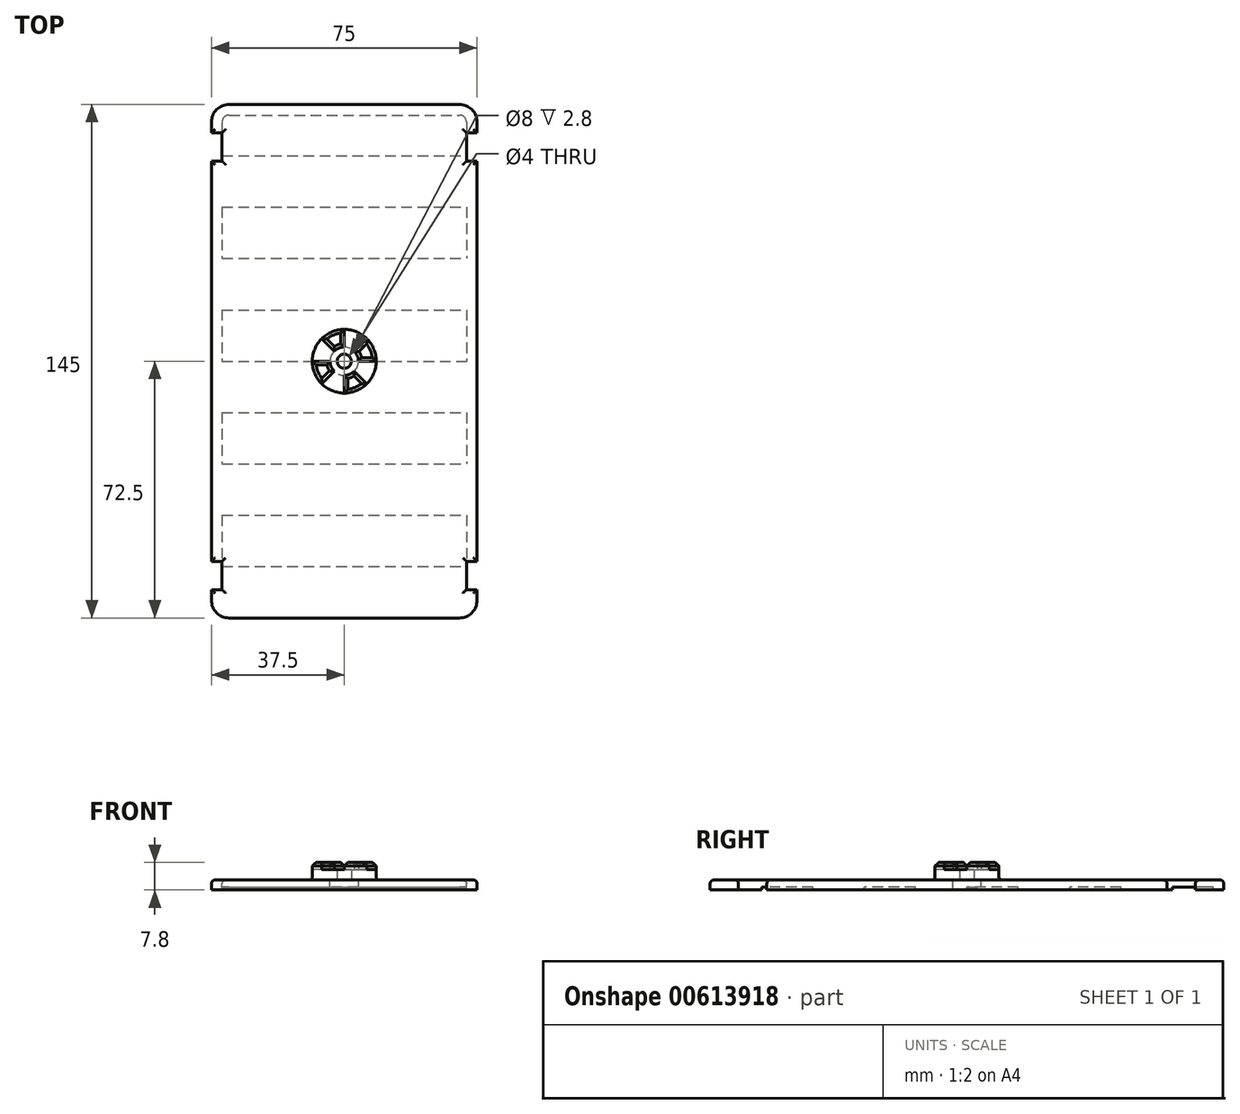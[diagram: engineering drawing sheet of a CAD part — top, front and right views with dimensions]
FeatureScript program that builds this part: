
annotation { "Feature Type Name" : "Feature", "Feature Type Description" : "" }
export const myFeature = defineFeature(function(context is Context, id is Id, definition is map)
    precondition{}
    {
        {
            var Q0;
            Q0=qCreatedBy(makeId("Top.planeOp"),FACE);
            var sketch = newSketch(context, id + "F0", { "sketchPlane" : qUnion([Q0])});
            skLineSegment(sketch, "E0.bottom", {"start": v(-32.5, 72.5) * mm, "end": v(32.5, 72.5) * mm});
            skLineSegment(sketch, "E0.top", {"start": v(-32.5, -72.5) * mm, "end": v(32.5, -72.5) * mm});
            skLineSegment(sketch, "E0.left", {"start": v(-37.5, 67.5) * mm, "end": v(-37.5, -67.5) * mm});
            skLineSegment(sketch, "E0.right", {"start": v(37.5, 67.5) * mm, "end": v(37.5, -67.5) * mm});
            skPoint(sketch, "E0.middle", {"position": v(0, 0) * mm});
            skLineSegment(sketch, "E1.0.1.0", {"start": v(-37.5, 58) * mm, "end": v(37.5, 58) * mm});
            skLineSegment(sketch, "E1.0.2.0", {"start": v(-37.5, 43.5) * mm, "end": v(37.5, 43.5) * mm});
            skLineSegment(sketch, "E1.0.3.0", {"start": v(-37.5, 29) * mm, "end": v(37.5, 29) * mm});
            skLineSegment(sketch, "E1.0.4.0", {"start": v(-37.5, 14.5) * mm, "end": v(37.5, 14.5) * mm});
            skLineSegment(sketch, "E1.0.5.0", {"start": v(-37.5, 0) * mm, "end": v(37.5, 0) * mm});
            skLineSegment(sketch, "E1.0.6.0", {"start": v(-37.5, -14.5) * mm, "end": v(37.5, -14.5) * mm});
            skLineSegment(sketch, "E1.0.7.0", {"start": v(-37.5, -29) * mm, "end": v(37.5, -29) * mm});
            skLineSegment(sketch, "E1.0.8.0", {"start": v(-37.5, -43.5) * mm, "end": v(37.5, -43.5) * mm});
            skLineSegment(sketch, "E1.0.9.0", {"start": v(-37.5, -58) * mm, "end": v(37.5, -58) * mm});
            skLineSegment(sketch, "E1.direction2", {"start": v(-37.5, 72.5) * mm, "end": v(-37.5, 58) * mm, "construction": true});
            skPoint(sketch, "E2.visualSharp", {"position": v(37.5, 72.5) * mm});
            skArc(sketch, "E2.filletArc", {"start": v(37.5, 67.5) * mm, "mid": v(36.04, 71.04) * mm, "end": v(32.5, 72.5) * mm});
            skPoint(sketch, "E3.visualSharp", {"position": v(-37.5, 72.5) * mm});
            skPoint(sketch, "E4.visualSharp", {"position": v(-37.5, -72.5) * mm});
            skArc(sketch, "E4.filletArc", {"start": v(-37.5, -67.5) * mm, "mid": v(-36.04, -71.04) * mm, "end": v(-32.5, -72.5) * mm});
            skPoint(sketch, "E5.visualSharp", {"position": v(37.5, -72.5) * mm});
            skArc(sketch, "E5.filletArc", {"start": v(32.5, -72.5) * mm, "mid": v(36.04, -71.04) * mm, "end": v(37.5, -67.5) * mm});
            skArc(sketch, "E6.filletArc", {"start": v(-32.5, 72.5) * mm, "mid": v(-36.04, 71.04) * mm, "end": v(-37.5, 67.5) * mm});
            skLineSegment(sketch, "E7.0", {"start": v(-34.5, 67.5) * mm, "end": v(-34.5, -67.5) * mm});
            skArc(sketch, "E7.1", {"start": v(-32.5, 69.5) * mm, "mid": v(-33.91, 68.91) * mm, "end": v(-34.5, 67.5) * mm});
            skArc(sketch, "E7.2", {"start": v(-34.5, -67.5) * mm, "mid": v(-33.91, -68.91) * mm, "end": v(-32.5, -69.5) * mm});
            skLineSegment(sketch, "E7.3", {"start": v(-32.5, 69.5) * mm, "end": v(32.5, 69.5) * mm});
            skLineSegment(sketch, "E7.4", {"start": v(-32.5, -69.5) * mm, "end": v(32.5, -69.5) * mm});
            skArc(sketch, "E7.5", {"start": v(32.5, -69.5) * mm, "mid": v(33.91, -68.91) * mm, "end": v(34.5, -67.5) * mm});
            skLineSegment(sketch, "E7.6", {"start": v(34.5, 67.5) * mm, "end": v(34.5, -67.5) * mm});
            skArc(sketch, "E7.7", {"start": v(34.5, 67.5) * mm, "mid": v(33.91, 68.91) * mm, "end": v(32.5, 69.5) * mm});
            skSolve(sketch);
        }
        {
            var Q0;
            {var subQ0=sQuery(id+"F0.wireOp",EDGE,"E1.0.3.0");Q0=makeQuery(id+"F0.imprint","IMPRINT",FACE,{"disambiguationData":[TD([[makeQuery(id+"F0.imprint","IMPRINT",EDGE,{"derivedFrom":subQ0}),-1.0]])]});}
            var Q1;
            {var subQ0=sQuery(id+"F0.wireOp",EDGE,"E1.0.5.0");Q1=makeQuery(id+"F0.imprint","IMPRINT",FACE,{"disambiguationData":[TD([[makeQuery(id+"F0.imprint","IMPRINT",EDGE,{"derivedFrom":subQ0}),-1.0]])]});}
            var Q2;
            {var subQ0=sQuery(id+"F0.wireOp",EDGE,"E1.0.7.0");Q2=makeQuery(id+"F0.imprint","IMPRINT",FACE,{"disambiguationData":[TD([[makeQuery(id+"F0.imprint","IMPRINT",EDGE,{"derivedFrom":subQ0}),-1.0]])]});}
            var Q3;
            {var subQ0=sQuery(id+"F0.wireOp",EDGE,"E0.top");Q3=makeQuery(id+"F0.imprint","IMPRINT",FACE,{"disambiguationData":[TD([[makeQuery(id+"F0.imprint","IMPRINT",EDGE,{"derivedFrom":subQ0}),1.0]])]});}
            var Q4;
            {var subQ0=sQuery(id+"F0.wireOp",EDGE,"E1.0.1.0");Q4=makeQuery(id+"F0.imprint","IMPRINT",FACE,{"disambiguationData":[TD([[makeQuery(id+"F0.imprint","IMPRINT",EDGE,{"derivedFrom":subQ0}),-1.0]])]});}
            var Q5;
            {var subQ0=sQuery(id+"F0.wireOp",EDGE,"E1.0.8.0");var subQ1=sQuery(id+"F0.wireOp",EDGE,"E0.left");var subQ2=makeQuery(id+"F0.imprint","INTERSECT",VERTEX,{"derivedFrom":[subQ1,subQ0]});Q5=makeQuery(id+"F0.imprint","IMPRINT",FACE,{"disambiguationData":[TD([[makeQuery(id+"F0.imprint","IMPRINT",EDGE,{"disambiguationData":[TD([[subQ2,-1.0]])],"derivedFrom":subQ1}),1.0]])]});}
            var Q6;
            {var subQ0=sQuery(id+"F0.wireOp",EDGE,"E1.0.8.0");var subQ1=sQuery(id+"F0.wireOp",EDGE,"E0.right");var subQ2=makeQuery(id+"F0.imprint","INTERSECT",VERTEX,{"derivedFrom":[subQ1,subQ0]});Q6=makeQuery(id+"F0.imprint","IMPRINT",FACE,{"disambiguationData":[TD([[makeQuery(id+"F0.imprint","IMPRINT",EDGE,{"disambiguationData":[TD([[subQ2,-1.0]])],"derivedFrom":subQ1}),-1.0]])]});}
            var Q7;
            {var subQ4=sQuery(id+"F0.wireOp",EDGE,"E7.2");Q7=makeQuery(id+"F0.imprint","IMPRINT",FACE,{"disambiguationData":[TD([[makeQuery(id+"F0.imprint","IMPRINT",EDGE,{"derivedFrom":subQ4}),1.0]])]});}
            var Q8;
            {var subQ0=sQuery(id+"F0.wireOp",EDGE,"E1.0.6.0");var subQ1=sQuery(id+"F0.wireOp",EDGE,"E0.right");var subQ2=makeQuery(id+"F0.imprint","INTERSECT",VERTEX,{"derivedFrom":[subQ1,subQ0]});Q8=makeQuery(id+"F0.imprint","IMPRINT",FACE,{"disambiguationData":[TD([[makeQuery(id+"F0.imprint","IMPRINT",EDGE,{"disambiguationData":[TD([[subQ2,-1.0]])],"derivedFrom":subQ1}),-1.0]])]});}
            var Q9;
            {var subQ0=sQuery(id+"F0.wireOp",EDGE,"E1.0.6.0");var subQ1=sQuery(id+"F0.wireOp",EDGE,"E0.left");var subQ2=makeQuery(id+"F0.imprint","INTERSECT",VERTEX,{"derivedFrom":[subQ1,subQ0]});Q9=makeQuery(id+"F0.imprint","IMPRINT",FACE,{"disambiguationData":[TD([[makeQuery(id+"F0.imprint","IMPRINT",EDGE,{"disambiguationData":[TD([[subQ2,-1.0]])],"derivedFrom":subQ1}),1.0]])]});}
            var Q10;
            {var subQ0=sQuery(id+"F0.wireOp",EDGE,"E1.0.4.0");var subQ1=sQuery(id+"F0.wireOp",EDGE,"E0.left");var subQ2=makeQuery(id+"F0.imprint","INTERSECT",VERTEX,{"derivedFrom":[subQ1,subQ0]});Q10=makeQuery(id+"F0.imprint","IMPRINT",FACE,{"disambiguationData":[TD([[makeQuery(id+"F0.imprint","IMPRINT",EDGE,{"disambiguationData":[TD([[subQ2,-1.0]])],"derivedFrom":subQ1}),1.0]])]});}
            var Q11;
            {var subQ0=sQuery(id+"F0.wireOp",EDGE,"E1.0.2.0");var subQ1=sQuery(id+"F0.wireOp",EDGE,"E0.left");var subQ2=makeQuery(id+"F0.imprint","INTERSECT",VERTEX,{"derivedFrom":[subQ1,subQ0]});Q11=makeQuery(id+"F0.imprint","IMPRINT",FACE,{"disambiguationData":[TD([[makeQuery(id+"F0.imprint","IMPRINT",EDGE,{"disambiguationData":[TD([[subQ2,-1.0]])],"derivedFrom":subQ1}),1.0]])]});}
            var Q12;
            Q12=makeQuery(id+"F0.imprint","IMPRINT",FACE,{"disambiguationData":[TD([[makeQuery(id+"F0.imprint","IMPRINT",EDGE,{"derivedFrom":sQuery(id+"F0.wireOp",EDGE,"E0.bottom")}),-1.0]])]});
            var Q13;
            {var subQ0=sQuery(id+"F0.wireOp",EDGE,"E1.0.4.0");var subQ1=sQuery(id+"F0.wireOp",EDGE,"E0.right");var subQ2=makeQuery(id+"F0.imprint","INTERSECT",VERTEX,{"derivedFrom":[subQ1,subQ0]});Q13=makeQuery(id+"F0.imprint","IMPRINT",FACE,{"disambiguationData":[TD([[makeQuery(id+"F0.imprint","IMPRINT",EDGE,{"disambiguationData":[TD([[subQ2,-1.0]])],"derivedFrom":subQ1}),-1.0]])]});}
            var Q14;
            {var subQ0=sQuery(id+"F0.wireOp",EDGE,"E1.0.2.0");var subQ1=sQuery(id+"F0.wireOp",EDGE,"E0.right");var subQ2=makeQuery(id+"F0.imprint","INTERSECT",VERTEX,{"derivedFrom":[subQ1,subQ0]});Q14=makeQuery(id+"F0.imprint","IMPRINT",FACE,{"disambiguationData":[TD([[makeQuery(id+"F0.imprint","IMPRINT",EDGE,{"disambiguationData":[TD([[subQ2,-1.0]])],"derivedFrom":subQ1}),-1.0]])]});}
            extrude(context, id + "F1", {"entities" : qUnion([Q0, Q1, Q2, Q3, Q4, Q5, Q6, Q7, Q8, Q9, Q10, Q11, Q12, Q13, Q14]), "depth" : -0.8 * mm, "offsetDistance" : 25 * mm});
        }
        {
            var Q0;
            Q0 = qSketchRegion(id + "F0", true);
            var Q1;
            {var subQ0=sQuery(id+"F0.wireOp",EDGE,"E7.1");Q1=makeQuery(id+"F0.imprint","IMPRINT",FACE,{"disambiguationData":[TD([[makeQuery(id+"F0.imprint","IMPRINT",EDGE,{"derivedFrom":subQ0}),1.0]])]});}
            var Q2;
            {var subQ0=sQuery(id+"F0.wireOp",EDGE,"E7.0");var subQ1=sQuery(id+"F0.wireOp",EDGE,"E1.0.2.0");var subQ2=makeQuery(id+"F0.imprint","INTERSECT",VERTEX,{"derivedFrom":[subQ1,subQ0]});Q2=makeQuery(id+"F0.imprint","IMPRINT",FACE,{"disambiguationData":[TD([[makeQuery(id+"F0.imprint","IMPRINT",EDGE,{"disambiguationData":[TD([[subQ2,-1.0]])],"derivedFrom":subQ1}),-1.0]])]});}
            var Q3;
            {var subQ0=sQuery(id+"F0.wireOp",EDGE,"E7.0");var subQ1=sQuery(id+"F0.wireOp",EDGE,"E1.0.1.0");var subQ2=makeQuery(id+"F0.imprint","INTERSECT",VERTEX,{"derivedFrom":[subQ1,subQ0]});Q3=makeQuery(id+"F0.imprint","IMPRINT",FACE,{"disambiguationData":[TD([[makeQuery(id+"F0.imprint","IMPRINT",EDGE,{"disambiguationData":[TD([[subQ2,-1.0]])],"derivedFrom":subQ1}),-1.0]])]});}
            var Q4;
            {var subQ0=sQuery(id+"F0.wireOp",EDGE,"E7.0");var subQ1=sQuery(id+"F0.wireOp",EDGE,"E1.0.3.0");var subQ2=makeQuery(id+"F0.imprint","INTERSECT",VERTEX,{"derivedFrom":[subQ1,subQ0]});Q4=makeQuery(id+"F0.imprint","IMPRINT",FACE,{"disambiguationData":[TD([[makeQuery(id+"F0.imprint","IMPRINT",EDGE,{"disambiguationData":[TD([[subQ2,-1.0]])],"derivedFrom":subQ1}),-1.0]])]});}
            var Q5;
            {var subQ0=sQuery(id+"F0.wireOp",EDGE,"E7.0");var subQ1=sQuery(id+"F0.wireOp",EDGE,"E1.0.4.0");var subQ2=makeQuery(id+"F0.imprint","INTERSECT",VERTEX,{"derivedFrom":[subQ1,subQ0]});Q5=makeQuery(id+"F0.imprint","IMPRINT",FACE,{"disambiguationData":[TD([[makeQuery(id+"F0.imprint","IMPRINT",EDGE,{"disambiguationData":[TD([[subQ2,-1.0]])],"derivedFrom":subQ1}),-1.0]])]});}
            var Q6;
            {var subQ0=sQuery(id+"F0.wireOp",EDGE,"E7.0");var subQ1=sQuery(id+"F0.wireOp",EDGE,"E1.0.5.0");var subQ2=makeQuery(id+"F0.imprint","INTERSECT",VERTEX,{"derivedFrom":[subQ1,subQ0]});Q6=makeQuery(id+"F0.imprint","IMPRINT",FACE,{"disambiguationData":[TD([[makeQuery(id+"F0.imprint","IMPRINT",EDGE,{"disambiguationData":[TD([[subQ2,-1.0]])],"derivedFrom":subQ1}),-1.0]])]});}
            var Q7;
            {var subQ4=sQuery(id+"F0.wireOp",EDGE,"E7.2");Q7=makeQuery(id+"F0.imprint","IMPRINT",FACE,{"disambiguationData":[TD([[makeQuery(id+"F0.imprint","IMPRINT",EDGE,{"derivedFrom":subQ4}),1.0]])]});}
            var Q8;
            {var subQ0=sQuery(id+"F0.wireOp",EDGE,"E7.0");var subQ1=sQuery(id+"F0.wireOp",EDGE,"E1.0.8.0");var subQ2=makeQuery(id+"F0.imprint","INTERSECT",VERTEX,{"derivedFrom":[subQ1,subQ0]});Q8=makeQuery(id+"F0.imprint","IMPRINT",FACE,{"disambiguationData":[TD([[makeQuery(id+"F0.imprint","IMPRINT",EDGE,{"disambiguationData":[TD([[subQ2,-1.0]])],"derivedFrom":subQ1}),-1.0]])]});}
            var Q9;
            {var subQ0=sQuery(id+"F0.wireOp",EDGE,"E7.0");var subQ1=sQuery(id+"F0.wireOp",EDGE,"E1.0.7.0");var subQ2=makeQuery(id+"F0.imprint","INTERSECT",VERTEX,{"derivedFrom":[subQ1,subQ0]});Q9=makeQuery(id+"F0.imprint","IMPRINT",FACE,{"disambiguationData":[TD([[makeQuery(id+"F0.imprint","IMPRINT",EDGE,{"disambiguationData":[TD([[subQ2,-1.0]])],"derivedFrom":subQ1}),-1.0]])]});}
            var Q10;
            {var subQ0=sQuery(id+"F0.wireOp",EDGE,"E7.0");var subQ1=sQuery(id+"F0.wireOp",EDGE,"E1.0.6.0");var subQ2=makeQuery(id+"F0.imprint","INTERSECT",VERTEX,{"derivedFrom":[subQ1,subQ0]});Q10=makeQuery(id+"F0.imprint","IMPRINT",FACE,{"disambiguationData":[TD([[makeQuery(id+"F0.imprint","IMPRINT",EDGE,{"disambiguationData":[TD([[subQ2,-1.0]])],"derivedFrom":subQ1}),-1.0]])]});}
            extrude(context, id + "F2", {"entities" : qUnion([Q0, Q1, Q2, Q3, Q4, Q5, Q6, Q7, Q8, Q9, Q10]), "operationType" : NewBodyOperationType.ADD, "depth" : 2 * mm, "offsetDistance" : 25 * mm});
        }
        {
            var Q0;
            Q0=makeQuery(id+"F2.opExtrude","CAP_FACE",FACE,{"disambiguationData":[OSD([sQuery(id+"F0.wireOp",EDGE,"E0.bottom"),sQuery(id+"F0.wireOp",EDGE,"E0.top"),sQuery(id+"F0.wireOp",EDGE,"E0.left"),sQuery(id+"F0.wireOp",EDGE,"E0.right")])],"isStart":false});
            var sketch = newSketch(context, id + "F3", { "sketchPlane" : qUnion([Q0])});
            skLineSegment(sketch, "E8.0", {"start": v(-37.5, 67.5) * mm, "end": v(-37.5, -67.5) * mm});
            skLineSegment(sketch, "E9.0", {"start": v(-32.5, 72.5) * mm, "end": v(32.5, 72.5) * mm});
            skLineSegment(sketch, "E10.0", {"start": v(37.5, 67.5) * mm, "end": v(37.5, -67.5) * mm});
            skLineSegment(sketch, "E11.0", {"start": v(-32.5, -72.5) * mm, "end": v(32.5, -72.5) * mm});
            skLineSegment(sketch, "E12.bottom", {"start": v(-29.5, -72.5) * mm, "end": v(-21.5, -72.5) * mm});
            skLineSegment(sketch, "E12.top", {"start": v(-29.5, -69.5) * mm, "end": v(-21.5, -69.5) * mm});
            skLineSegment(sketch, "E12.left", {"start": v(-29.5, -72.5) * mm, "end": v(-29.5, -69.5) * mm});
            skLineSegment(sketch, "E12.right", {"start": v(-21.5, -72.5) * mm, "end": v(-21.5, -69.5) * mm});
            skLineSegment(sketch, "E13.bottom", {"start": v(21.5, -72.5) * mm, "end": v(29.5, -72.5) * mm});
            skLineSegment(sketch, "E13.top", {"start": v(21.5, -69.5) * mm, "end": v(29.5, -69.5) * mm});
            skLineSegment(sketch, "E13.left", {"start": v(21.5, -72.5) * mm, "end": v(21.5, -69.5) * mm});
            skLineSegment(sketch, "E13.right", {"start": v(29.5, -72.5) * mm, "end": v(29.5, -69.5) * mm});
            skLineSegment(sketch, "E14.bottom", {"start": v(37.5, -64.5) * mm, "end": v(34.5, -64.5) * mm});
            skLineSegment(sketch, "E14.top", {"start": v(37.5, -56.5) * mm, "end": v(34.5, -56.5) * mm});
            skLineSegment(sketch, "E14.left", {"start": v(37.5, -64.5) * mm, "end": v(37.5, -56.5) * mm});
            skLineSegment(sketch, "E14.right", {"start": v(34.5, -64.5) * mm, "end": v(34.5, -56.5) * mm});
            skLineSegment(sketch, "E15.bottom", {"start": v(-37.5, -64.5) * mm, "end": v(-34.5, -64.5) * mm});
            skLineSegment(sketch, "E15.top", {"start": v(-37.5, -56.5) * mm, "end": v(-34.5, -56.5) * mm});
            skLineSegment(sketch, "E15.left", {"start": v(-37.5, -64.5) * mm, "end": v(-37.5, -56.5) * mm});
            skLineSegment(sketch, "E15.right", {"start": v(-34.5, -64.5) * mm, "end": v(-34.5, -56.5) * mm});
            skLineSegment(sketch, "E16.bottom", {"start": v(-37.5, 56.5) * mm, "end": v(-34.5, 56.5) * mm});
            skLineSegment(sketch, "E16.top", {"start": v(-37.5, 64.5) * mm, "end": v(-34.5, 64.5) * mm});
            skLineSegment(sketch, "E16.left", {"start": v(-37.5, 56.5) * mm, "end": v(-37.5, 64.5) * mm});
            skLineSegment(sketch, "E16.right", {"start": v(-34.5, 56.5) * mm, "end": v(-34.5, 64.5) * mm});
            skLineSegment(sketch, "E17.bottom", {"start": v(-29.5, 72.5) * mm, "end": v(-21.5, 72.5) * mm});
            skLineSegment(sketch, "E17.top", {"start": v(-29.5, 69.5) * mm, "end": v(-21.5, 69.5) * mm});
            skLineSegment(sketch, "E17.left", {"start": v(-29.5, 72.5) * mm, "end": v(-29.5, 69.5) * mm});
            skLineSegment(sketch, "E17.right", {"start": v(-21.5, 72.5) * mm, "end": v(-21.5, 69.5) * mm});
            skLineSegment(sketch, "E18.bottom", {"start": v(21.5, 72.5) * mm, "end": v(29.5, 72.5) * mm});
            skLineSegment(sketch, "E18.top", {"start": v(21.5, 69.5) * mm, "end": v(29.5, 69.5) * mm});
            skLineSegment(sketch, "E18.left", {"start": v(21.5, 72.5) * mm, "end": v(21.5, 69.5) * mm});
            skLineSegment(sketch, "E18.right", {"start": v(29.5, 72.5) * mm, "end": v(29.5, 69.5) * mm});
            skCircle(sketch, "E19", {"center": v(0, 0) * mm, "radius": 2 * mm});
            skCircle(sketch, "E20", {"center": v(0, 0) * mm, "radius": 4 * mm});
            skCircle(sketch, "E21", {"center": v(0, 0) * mm, "radius": 9 * mm});
            skLineSegment(sketch, "E22.bottom", {"start": v(37.5, 64.5) * mm, "end": v(34.5, 64.5) * mm});
            skLineSegment(sketch, "E22.top", {"start": v(37.5, 56.5) * mm, "end": v(34.5, 56.5) * mm});
            skLineSegment(sketch, "E22.left", {"start": v(37.5, 64.5) * mm, "end": v(37.5, 56.5) * mm});
            skLineSegment(sketch, "E22.right", {"start": v(34.5, 64.5) * mm, "end": v(34.5, 56.5) * mm});
            skSolve(sketch);
        }
        {
            var Q0;
            Q0=makeQuery(id+"F3.imprint","IMPRINT",FACE,{"disambiguationData":[TD([[makeQuery(id+"F3.imprint","IMPRINT",EDGE,{"derivedFrom":sQuery(id+"F3.wireOp",EDGE,"E13.bottom")}),1.0]])]});
            var Q1;
            Q1=makeQuery(id+"F3.imprint","IMPRINT",FACE,{"disambiguationData":[TD([[makeQuery(id+"F3.imprint","IMPRINT",EDGE,{"derivedFrom":sQuery(id+"F3.wireOp",EDGE,"E14.bottom")}),-1.0]])]});
            var Q2;
            Q2=makeQuery(id+"F3.imprint","IMPRINT",FACE,{"disambiguationData":[TD([[makeQuery(id+"F3.imprint","IMPRINT",EDGE,{"derivedFrom":sQuery(id+"F3.wireOp",EDGE,"E15.bottom")}),1.0]])]});
            var Q3;
            Q3=makeQuery(id+"F3.imprint","IMPRINT",FACE,{"disambiguationData":[TD([[makeQuery(id+"F3.imprint","IMPRINT",EDGE,{"derivedFrom":sQuery(id+"F3.wireOp",EDGE,"E12.bottom")}),1.0]])]});
            var Q4;
            Q4=makeQuery(id+"F3.imprint","IMPRINT",FACE,{"disambiguationData":[TD([[makeQuery(id+"F3.imprint","IMPRINT",EDGE,{"derivedFrom":sQuery(id+"F3.wireOp",EDGE,"E18.bottom")}),-1.0]])]});
            var Q5;
            Q5=makeQuery(id+"F3.imprint","IMPRINT",FACE,{"disambiguationData":[TD([[makeQuery(id+"F3.imprint","IMPRINT",EDGE,{"derivedFrom":sQuery(id+"F3.wireOp",EDGE,"B49sznqi-fGRp-VqjG-tYYg-6xHxRTEvqkHY.bottom")}),1.0]])]});
            var Q6;
            Q6=makeQuery(id+"F3.imprint","IMPRINT",FACE,{"disambiguationData":[TD([[makeQuery(id+"F3.imprint","IMPRINT",EDGE,{"derivedFrom":sQuery(id+"F3.wireOp",EDGE,"E17.bottom")}),-1.0]])]});
            var Q7;
            Q7=makeQuery(id+"F3.imprint","IMPRINT",FACE,{"disambiguationData":[TD([[makeQuery(id+"F3.imprint","IMPRINT",EDGE,{"derivedFrom":sQuery(id+"F3.wireOp",EDGE,"E16.bottom")}),1.0]])]});
            var Q8;
            Q8=makeQuery(id+"F3.imprint","IMPRINT",FACE,{"disambiguationData":[TD([[makeQuery(id+"F3.imprint","IMPRINT",EDGE,{"derivedFrom":sQuery(id+"F3.wireOp",EDGE,"E19")}),-1.0]])]});
            var Q9;
            Q9=makeQuery(id+"F3.imprint","IMPRINT",FACE,{"disambiguationData":[TD([[makeQuery(id+"F3.imprint","IMPRINT",EDGE,{"derivedFrom":sQuery(id+"F3.wireOp",EDGE,"E19")}),1.0]])]});
            var Q10;
            Q10=makeQuery(id+"F3.imprint","IMPRINT",FACE,{"disambiguationData":[TD([[makeQuery(id+"F3.imprint","IMPRINT",EDGE,{"derivedFrom":sQuery(id+"F3.wireOp",EDGE,"E22.bottom")}),1.0]])]});
            extrude(context, id + "F4", {"entities" : qUnion([Q0, Q1, Q2, Q3, Q4, Q5, Q6, Q7, Q8, Q9, Q10]), "operationType" : NewBodyOperationType.REMOVE, "oppositeDirection" : true, "depth" : 5 * mm, "offsetDistance" : 25 * mm});
        }
        {
            var Q0;
            Q0=makeQuery(id+"F3.imprint","IMPRINT",FACE,{"disambiguationData":[TD([[makeQuery(id+"F3.imprint","IMPRINT",EDGE,{"derivedFrom":sQuery(id+"F3.wireOp",EDGE,"E20")}),-1.0]])]});
            var Q1;
            Q1=makeQuery(id+"F3.imprint","IMPRINT",FACE,{"disambiguationData":[TD([[makeQuery(id+"F3.imprint","IMPRINT",EDGE,{"derivedFrom":sQuery(id+"F3.wireOp",EDGE,"E19")}),-1.0]])]});
            extrude(context, id + "F5", {"entities" : qUnion([Q0, Q1]), "operationType" : NewBodyOperationType.ADD, "depth" : 3 * mm, "offsetDistance" : 25 * mm});
        }
        {
            var Q0;
            Q0=makeQuery(id+"F5.opExtrude","CAP_FACE",FACE,{"disambiguationData":[OSD([sQuery(id+"F3.wireOp",EDGE,"E20"),sQuery(id+"F3.wireOp",EDGE,"E21")])],"isStart":false});
            var sketch = newSketch(context, id + "F6", { "sketchPlane" : qUnion([Q0])});
            skCircle(sketch, "E23.0", {"center": v(0, 0) * mm, "radius": 9 * mm});
            skCircle(sketch, "E24.0", {"center": v(0, 0) * mm, "radius": 4 * mm});
            skLineSegment(sketch, "E25", {"start": v(0, 4) * mm, "end": v(0, 9) * mm});
            skLineSegment(sketch, "E26.1.0", {"start": v(-2.83, 2.83) * mm, "end": v(-6.36, 6.36) * mm});
            skLineSegment(sketch, "E26.2.0", {"start": v(-4, 0) * mm, "end": v(-9, 0) * mm});
            skLineSegment(sketch, "E26.3.0", {"start": v(-2.83, -2.83) * mm, "end": v(-6.36, -6.36) * mm});
            skLineSegment(sketch, "E26.4.0", {"start": v(0, -4) * mm, "end": v(0, -9) * mm});
            skLineSegment(sketch, "E26.5.0", {"start": v(2.83, -2.83) * mm, "end": v(6.36, -6.36) * mm});
            skLineSegment(sketch, "E26.6.0", {"start": v(4, 0) * mm, "end": v(9, 0) * mm});
            skLineSegment(sketch, "E26.7.0", {"start": v(2.83, 2.83) * mm, "end": v(6.36, 6.36) * mm});
            skSolve(sketch);
        }
        {
            var Q0;
            {var subQ0=sQuery(id+"F6.wireOp",EDGE,"E26.6.0");Q0=makeQuery(id+"F6.imprint","IMPRINT",FACE,{"disambiguationData":[TD([[makeQuery(id+"F6.imprint","IMPRINT",EDGE,{"derivedFrom":subQ0}),1.0]])]});}
            var Q1;
            {var subQ0=sQuery(id+"F6.wireOp",EDGE,"E26.4.0");Q1=makeQuery(id+"F6.imprint","IMPRINT",FACE,{"disambiguationData":[TD([[makeQuery(id+"F6.imprint","IMPRINT",EDGE,{"derivedFrom":subQ0}),1.0]])]});}
            var Q2;
            {var subQ0=sQuery(id+"F6.wireOp",EDGE,"E25");Q2=makeQuery(id+"F6.imprint","IMPRINT",FACE,{"disambiguationData":[TD([[makeQuery(id+"F6.imprint","IMPRINT",EDGE,{"derivedFrom":subQ0}),1.0]])]});}
            var Q3;
            {var subQ0=sQuery(id+"F6.wireOp",EDGE,"E26.2.0");Q3=makeQuery(id+"F6.imprint","IMPRINT",FACE,{"disambiguationData":[TD([[makeQuery(id+"F6.imprint","IMPRINT",EDGE,{"derivedFrom":subQ0}),1.0]])]});}
            extrude(context, id + "F7", {"entities" : qUnion([Q0, Q1, Q2, Q3]), "operationType" : NewBodyOperationType.ADD, "depth" : 2 * mm, "offsetDistance" : 25 * mm});
        }
        {
            var Q0;
            Q0=makeQuery(id+"F7.opExtrude","CAP_EDGE",EDGE,{"disambiguationData":[OSD([sQuery(id+"F6.wireOp",EDGE,"E26.1.0")])],"isStart":false});
            var Q1;
            Q1=makeQuery(id+"F7.opExtrude","CAP_EDGE",EDGE,{"disambiguationData":[OSD([sQuery(id+"F6.wireOp",EDGE,"E25")])],"isStart":false});
            var Q2;
            Q2=makeQuery(id+"F7.opExtrude","CAP_EDGE",EDGE,{"disambiguationData":[OSD([sQuery(id+"F6.wireOp",EDGE,"E26.7.0")])],"isStart":false});
            var Q3;
            Q3=makeQuery(id+"F7.opExtrude","CAP_EDGE",EDGE,{"disambiguationData":[OSD([sQuery(id+"F6.wireOp",EDGE,"E26.6.0")])],"isStart":false});
            var Q4;
            Q4=makeQuery(id+"F7.opExtrude","CAP_EDGE",EDGE,{"disambiguationData":[OSD([sQuery(id+"F6.wireOp",EDGE,"E26.5.0")])],"isStart":false});
            var Q5;
            Q5=makeQuery(id+"F7.opExtrude","CAP_EDGE",EDGE,{"disambiguationData":[OSD([sQuery(id+"F6.wireOp",EDGE,"E26.4.0")])],"isStart":false});
            var Q6;
            Q6=makeQuery(id+"F7.opExtrude","CAP_EDGE",EDGE,{"disambiguationData":[OSD([sQuery(id+"F6.wireOp",EDGE,"E26.3.0")])],"isStart":false});
            var Q7;
            Q7=makeQuery(id+"F7.opExtrude","CAP_EDGE",EDGE,{"disambiguationData":[OSD([sQuery(id+"F6.wireOp",EDGE,"E26.2.0")])],"isStart":false});
            var Q8;
            {var subQ0=sQuery(id+"F6.wireOp",EDGE,"E23.0");Q8=makeQuery(id+"F7.opExtrude","CAP_EDGE",EDGE,{"disambiguationData":[OSD([subQ0]),TDD([makeQuery(id+"F6.imprint","IMPRINT",EDGE,{"disambiguationData":[TD([[makeQuery(id+"F6.imprint","INTERSECT",VERTEX,{"derivedFrom":[subQ0,sQuery(id+"F6.wireOp",EDGE,"E26.6.0")]}),-1.0]])],"derivedFrom":subQ0})])],"isStart":false});}
            var Q9;
            {var subQ0=sQuery(id+"F6.wireOp",EDGE,"E24.0");Q9=makeQuery(id+"F7.opExtrude","CAP_EDGE",EDGE,{"disambiguationData":[OSD([subQ0]),TDD([makeQuery(id+"F6.imprint","IMPRINT",EDGE,{"disambiguationData":[TD([[makeQuery(id+"F6.imprint","INTERSECT",VERTEX,{"derivedFrom":[subQ0,sQuery(id+"F6.wireOp",EDGE,"E26.6.0")]}),-1.0]])],"derivedFrom":subQ0})])],"isStart":false});}
            var Q10;
            {var subQ0=sQuery(id+"F6.wireOp",EDGE,"E24.0");Q10=makeQuery(id+"F7.opExtrude","CAP_EDGE",EDGE,{"disambiguationData":[OSD([subQ0]),TDD([makeQuery(id+"F6.imprint","IMPRINT",EDGE,{"disambiguationData":[TD([[makeQuery(id+"F6.imprint","INTERSECT",VERTEX,{"derivedFrom":[subQ0,sQuery(id+"F6.wireOp",EDGE,"E25")]}),-1.0]])],"derivedFrom":subQ0})])],"isStart":false});}
            var Q11;
            {var subQ0=sQuery(id+"F6.wireOp",EDGE,"E24.0");Q11=makeQuery(id+"F7.opExtrude","CAP_EDGE",EDGE,{"disambiguationData":[OSD([subQ0]),TDD([makeQuery(id+"F6.imprint","IMPRINT",EDGE,{"disambiguationData":[TD([[makeQuery(id+"F6.imprint","INTERSECT",VERTEX,{"derivedFrom":[subQ0,sQuery(id+"F6.wireOp",EDGE,"E26.2.0")]}),-1.0]])],"derivedFrom":subQ0})])],"isStart":false});}
            var Q12;
            {var subQ0=sQuery(id+"F6.wireOp",EDGE,"E23.0");Q12=makeQuery(id+"F7.opExtrude","CAP_EDGE",EDGE,{"disambiguationData":[OSD([subQ0]),TDD([makeQuery(id+"F6.imprint","IMPRINT",EDGE,{"disambiguationData":[TD([[makeQuery(id+"F6.imprint","INTERSECT",VERTEX,{"derivedFrom":[subQ0,sQuery(id+"F6.wireOp",EDGE,"E26.2.0")]}),-1.0]])],"derivedFrom":subQ0})])],"isStart":false});}
            var Q13;
            {var subQ0=sQuery(id+"F6.wireOp",EDGE,"E24.0");Q13=makeQuery(id+"F7.opExtrude","CAP_EDGE",EDGE,{"disambiguationData":[OSD([subQ0]),TDD([makeQuery(id+"F6.imprint","IMPRINT",EDGE,{"disambiguationData":[TD([[makeQuery(id+"F6.imprint","INTERSECT",VERTEX,{"derivedFrom":[subQ0,sQuery(id+"F6.wireOp",EDGE,"E26.4.0")]}),-1.0]])],"derivedFrom":subQ0})])],"isStart":false});}
            var Q14;
            {var subQ0=sQuery(id+"F6.wireOp",EDGE,"E23.0");Q14=makeQuery(id+"F7.opExtrude","CAP_EDGE",EDGE,{"disambiguationData":[OSD([subQ0]),TDD([makeQuery(id+"F6.imprint","IMPRINT",EDGE,{"disambiguationData":[TD([[makeQuery(id+"F6.imprint","INTERSECT",VERTEX,{"derivedFrom":[subQ0,sQuery(id+"F6.wireOp",EDGE,"E26.4.0")]}),-1.0]])],"derivedFrom":subQ0})])],"isStart":false});}
            var Q15;
            Q15=makeQuery(id+"F7.opExtrude","CAP_EDGE",EDGE,{"disambiguationData":[OSD([sQuery(id+"F6.wireOp",EDGE,"E26.3.0")])],"isStart":true});
            var Q16;
            Q16=makeQuery(id+"F7.opExtrude","CAP_EDGE",EDGE,{"disambiguationData":[OSD([sQuery(id+"F6.wireOp",EDGE,"E26.4.0")])],"isStart":true});
            var Q17;
            Q17=makeQuery(id+"F7.opExtrude","CAP_EDGE",EDGE,{"disambiguationData":[OSD([sQuery(id+"F6.wireOp",EDGE,"E26.6.0")])],"isStart":true});
            var Q18;
            Q18=makeQuery(id+"F7.opExtrude","CAP_EDGE",EDGE,{"disambiguationData":[OSD([sQuery(id+"F6.wireOp",EDGE,"E26.5.0")])],"isStart":true});
            var Q19;
            Q19=makeQuery(id+"F7.opExtrude","CAP_EDGE",EDGE,{"disambiguationData":[OSD([sQuery(id+"F6.wireOp",EDGE,"E25")])],"isStart":true});
            var Q20;
            Q20=makeQuery(id+"F7.opExtrude","CAP_EDGE",EDGE,{"disambiguationData":[OSD([sQuery(id+"F6.wireOp",EDGE,"E26.7.0")])],"isStart":true});
            var Q21;
            Q21=makeQuery(id+"F7.opExtrude","CAP_EDGE",EDGE,{"disambiguationData":[OSD([sQuery(id+"F6.wireOp",EDGE,"E26.2.0")])],"isStart":true});
            var Q22;
            {var subQ0=sQuery(id+"F6.wireOp",EDGE,"E23.0");Q22=makeQuery(id+"F7.opExtrude","CAP_EDGE",EDGE,{"disambiguationData":[OSD([subQ0]),TDD([makeQuery(id+"F6.imprint","IMPRINT",EDGE,{"disambiguationData":[TD([[makeQuery(id+"F6.imprint","INTERSECT",VERTEX,{"derivedFrom":[subQ0,sQuery(id+"F6.wireOp",EDGE,"E25")]}),-1.0]])],"derivedFrom":subQ0})])],"isStart":false});}
            var Q23;
            Q23=makeQuery(id+"F7.opExtrude","CAP_EDGE",EDGE,{"disambiguationData":[OSD([sQuery(id+"F6.wireOp",EDGE,"E26.1.0")])],"isStart":true});
            chamfer(context, id + "F8", {"entities" : qUnion([Q0, Q1, Q2, Q3, Q4, Q5, Q6, Q7, Q8, Q9, Q10, Q11, Q12, Q13, Q14, Q15, Q16, Q17, Q18, Q19, Q20, Q21, Q22, Q23]), "width" : 1 * mm, "tangentPropagation" : true});
        }
        {
            var Q0;
            Q0=makeQuery(id+"F2.opExtrude","CAP_FACE",FACE,{"disambiguationData":[OSD([sQuery(id+"F0.wireOp",EDGE,"E0.bottom"),sQuery(id+"F0.wireOp",EDGE,"E0.top"),sQuery(id+"F0.wireOp",EDGE,"E0.left"),sQuery(id+"F0.wireOp",EDGE,"E0.right"),sQuery(id+"F0.wireOp",EDGE,"E2.filletArc"),sQuery(id+"F0.wireOp",EDGE,"E4.filletArc"),sQuery(id+"F0.wireOp",EDGE,"E5.filletArc"),sQuery(id+"F0.wireOp",EDGE,"E6.filletArc")])],"isStart":false});
            fillet(context, id + "F9", {"entities" : qUnion([Q0]), "radius" : 1 * mm, "tangentPropagation" : true, "allowEdgeOverflow" : false});
        }
    });
